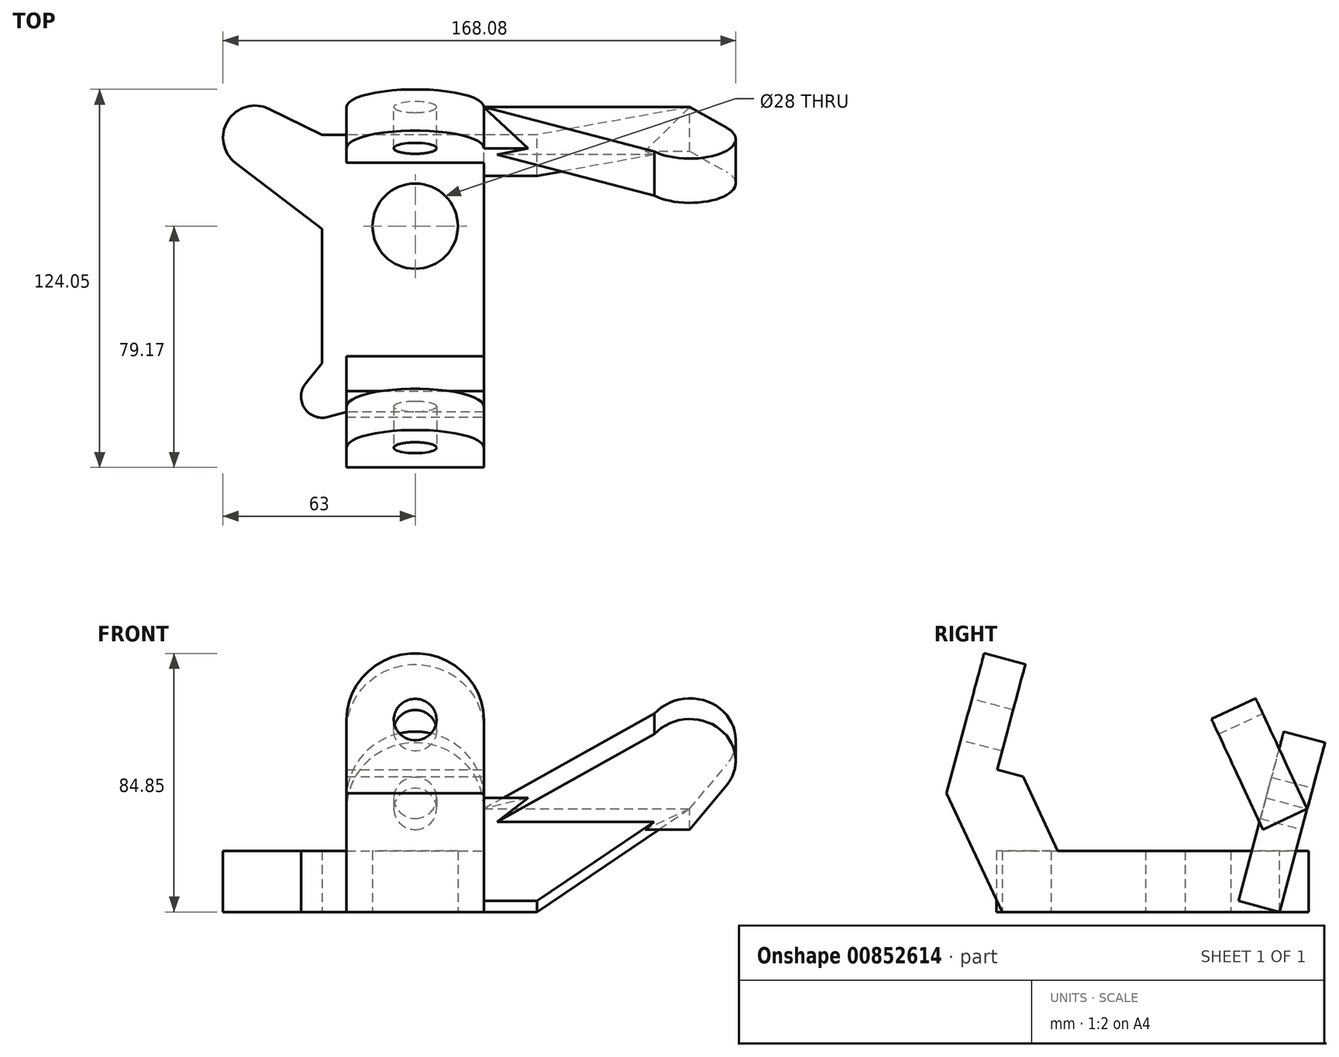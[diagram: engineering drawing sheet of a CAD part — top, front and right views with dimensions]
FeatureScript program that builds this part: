
annotation { "Feature Type Name" : "Feature", "Feature Type Description" : "" }
export const myFeature = defineFeature(function(context is Context, id is Id, definition is map)
    precondition{}
    {
        {
            var Q0;
            Q0=qCreatedBy(makeId("Top.planeOp"),FACE);
            var sketch = newSketch(context, id + "F0", { "sketchPlane" : qUnion([Q0])});
            skCircle(sketch, "E0", {"center": v(0, 15.5) * mm, "radius": 14 * mm});
            skLineSegment(sketch, "E1.bottom", {"start": v(22.5, 45.5) * mm, "end": v(-22.5, 45.5) * mm});
            skLineSegment(sketch, "E1.top", {"start": v(22.5, -45.5) * mm, "end": v(-22.5, -45.5) * mm});
            skLineSegment(sketch, "E1.left", {"start": v(22.5, 45.5) * mm, "end": v(22.5, -45.5) * mm});
            skLineSegment(sketch, "E1.right", {"start": v(-22.5, 45.5) * mm, "end": v(-22.5, -45.5) * mm});
            skPoint(sketch, "E1.middle", {"position": v(0, 0) * mm});
            skCircle(sketch, "E2", {"center": v(-52.5, 44.55) * mm, "radius": 10.5 * mm});
            skCircle(sketch, "E3", {"center": v(-30.5, -40.45) * mm, "radius": 6.91 * mm});
            skLineSegment(sketch, "E4", {"start": v(-30.5, -40.45) * mm, "end": v(-30.5, 14.55) * mm});
            skLineSegment(sketch, "E5", {"start": v(-30.5, 14.55) * mm, "end": v(-58.87, 36.2) * mm});
            skLineSegment(sketch, "E6", {"start": v(-30.5, 14.55) * mm, "end": v(-30.5, 45.5) * mm});
            skLineSegment(sketch, "E7", {"start": v(-30.5, 45.5) * mm, "end": v(-47.9, 53.98) * mm});
            skLineSegment(sketch, "E8", {"start": v(-30.5, 45.5) * mm, "end": v(-22.5, 45.5) * mm});
            skLineSegment(sketch, "E9", {"start": v(-30.5, -29.5) * mm, "end": v(-35.86, -36.1) * mm});
            skLineSegment(sketch, "E10", {"start": v(-22.5, -45.5) * mm, "end": v(-28.74, -47.14) * mm});
            skSolve(sketch);
        }
        {
            var Q0;
            {var subQ0=sQuery(id+"F0.wireOp",EDGE,"E5");Q0=makeQuery(id+"F0.imprint","IMPRINT",FACE,{"disambiguationData":[TD([[makeQuery(id+"F0.imprint","IMPRINT",EDGE,{"derivedFrom":subQ0}),-1.0]])]});}
            var Q1;
            {var subQ0=sQuery(id+"F0.wireOp",EDGE,"E2");var subQ1=makeQuery(id+"F0.imprint","INTERSECT",VERTEX,{"derivedFrom":[subQ0,sQuery(id+"F0.wireOp",EDGE,"E5")]});Q1=makeQuery(id+"F0.imprint","IMPRINT",FACE,{"disambiguationData":[TD([[makeQuery(id+"F0.imprint","IMPRINT",EDGE,{"disambiguationData":[TD([[subQ1,1.0]])],"derivedFrom":subQ0}),1.0]])]});}
            var Q2;
            Q2=makeQuery(id+"F0.imprint","IMPRINT",FACE,{"disambiguationData":[TD([[makeQuery(id+"F0.imprint","IMPRINT",EDGE,{"derivedFrom":sQuery(id+"F0.wireOp",EDGE,"E0")}),-1.0]])]});
            var Q3;
            Q3=makeQuery(id+"F0.imprint","IMPRINT",FACE,{"disambiguationData":[TD([[makeQuery(id+"F0.imprint","IMPRINT",EDGE,{"derivedFrom":sQuery(id+"F0.wireOp",EDGE,"E1.right")}),-1.0]])]});
            var Q4;
            {var subQ0=sQuery(id+"F0.wireOp",EDGE,"E3");var subQ1=makeQuery(id+"F0.imprint","INTERSECT",VERTEX,{"derivedFrom":[subQ0,sQuery(id+"F0.wireOp",EDGE,"E9")]});Q4=makeQuery(id+"F0.imprint","IMPRINT",FACE,{"disambiguationData":[TD([[makeQuery(id+"F0.imprint","IMPRINT",EDGE,{"disambiguationData":[TD([[subQ1,1.0]])],"derivedFrom":subQ0}),1.0]])]});}
            var Q5;
            {var subQ0=sQuery(id+"F0.wireOp",EDGE,"E9");Q5=makeQuery(id+"F0.imprint","IMPRINT",FACE,{"disambiguationData":[TD([[makeQuery(id+"F0.imprint","IMPRINT",EDGE,{"derivedFrom":subQ0}),1.0]])]});}
            extrude(context, id + "F1", {"entities" : qUnion([Q0, Q1, Q2, Q3, Q4, Q5]), "depth" : 20 * mm, "offsetDistance" : 25 * mm});
        }
        {
            var Q0;
            Q0=makeQuery(id+"F1.opExtrude","CAP_EDGE",EDGE,{"disambiguationData":[OSD([sQuery(id+"F0.wireOp",EDGE,"E1.bottom"),sQuery(id+"F0.wireOp",EDGE,"E8")])],"isStart":true});
            cPlane(context, id + "F2", {"entities" : qUnion([Q0]), "cplaneType" : CPlaneType.LINE_ANGLE, "offset" : 25 * mm, "angle" : 15 * degree, "width" : 150 * mm, "height" : 150 * mm});
        }
        {
            var Q0;
            Q0=qCreatedBy(id+"F2.planeOp",FACE);
            var sketch = newSketch(context, id + "F3", { "sketchPlane" : qUnion([Q0])});
            skCircle(sketch, "E11", {"center": v(0, 46.78) * mm, "radius": 22.5 * mm});
            skLineSegment(sketch, "E12", {"start": v(-22.5, 46.78) * mm, "end": v(-22.5, 11.78) * mm});
            skLineSegment(sketch, "E13", {"start": v(22.5, 46.78) * mm, "end": v(22.5, 11.78) * mm});
            skLineSegment(sketch, "E14", {"start": v(22.5, 11.78) * mm, "end": v(-22.5, 11.78) * mm});
            skCircle(sketch, "E15", {"center": v(0, 46.78) * mm, "radius": 7 * mm});
            skLineSegment(sketch, "E16", {"start": v(22.5, 46.78) * mm, "end": v(90, 46.78) * mm});
            skLineSegment(sketch, "E17", {"start": v(22.5, 11.78) * mm, "end": v(40, 11.78) * mm});
            skLineSegment(sketch, "E18", {"start": v(90, 46.78) * mm, "end": v(40, 11.78) * mm});
            skSolve(sketch);
        }
        {
            var Q0;
            Q0=makeQuery(id+"F3.imprint","IMPRINT",FACE,{"disambiguationData":[TD([[makeQuery(id+"F3.imprint","IMPRINT",EDGE,{"derivedFrom":sQuery(id+"F3.wireOp",EDGE,"E15")}),-1.0]])]});
            var Q1;
            {var subQ0=sQuery(id+"F3.wireOp",EDGE,"E12");Q1=makeQuery(id+"F3.imprint","IMPRINT",FACE,{"disambiguationData":[TD([[makeQuery(id+"F3.imprint","IMPRINT",EDGE,{"derivedFrom":subQ0}),1.0]])]});}
            var Q2;
            Q2=makeQuery(id+"F3.imprint","IMPRINT",FACE,{"disambiguationData":[TD([[makeQuery(id+"F3.imprint","IMPRINT",EDGE,{"derivedFrom":sQuery(id+"F3.wireOp",EDGE,"E13")}),1.0]])]});
            extrude(context, id + "F4", {"entities" : qUnion([Q0, Q1, Q2]), "operationType" : NewBodyOperationType.ADD, "depth" : 14 * mm, "offsetDistance" : 25 * mm});
        }
        {
            var Q0;
            Q0=makeQuery(id+"F4.opExtrude","CAP_EDGE",EDGE,{"disambiguationData":[OSD([sQuery(id+"F3.wireOp",EDGE,"E16")])],"isStart":true});
            cPlane(context, id + "F5", {"entities" : qUnion([Q0]), "cplaneType" : CPlaneType.LINE_ANGLE, "offset" : 25 * mm, "angle" : 25 * degree, "width" : 150 * mm, "height" : 150 * mm});
        }
        {
            var Q0;
            Q0=qCreatedBy(id+"F5.planeOp",FACE);
            var sketch = newSketch(context, id + "F6", { "sketchPlane" : qUnion([Q0])});
            skCircle(sketch, "E19", {"center": v(-90.08, 32.58) * mm, "radius": 15 * mm});
            skLineSegment(sketch, "E20", {"start": v(-90, 7.58) * mm, "end": v(-102.05, 23.54) * mm});
            skLineSegment(sketch, "E21", {"start": v(-78.48, 42.1) * mm, "end": v(-22.44, 7.58) * mm});
            skLineSegment(sketch, "E22", {"start": v(-22.44, 7.58) * mm, "end": v(-90, 7.58) * mm});
            skSolve(sketch);
        }
        {
            var Q0;
            {var subQ0=sQuery(id+"F6.wireOp",EDGE,"E20");Q0=makeQuery(id+"F6.imprint","IMPRINT",FACE,{"disambiguationData":[TD([[makeQuery(id+"F6.imprint","IMPRINT",EDGE,{"derivedFrom":subQ0}),-1.0]])]});}
            var Q1;
            {var subQ0=sQuery(id+"F6.wireOp",EDGE,"E19");var subQ1=makeQuery(id+"F6.imprint","INTERSECT",VERTEX,{"derivedFrom":[subQ0,sQuery(id+"F6.wireOp",EDGE,"E20")]});Q1=makeQuery(id+"F6.imprint","IMPRINT",FACE,{"disambiguationData":[TD([[makeQuery(id+"F6.imprint","IMPRINT",EDGE,{"disambiguationData":[TD([[subQ1,1.0]])],"derivedFrom":subQ0}),1.0]])]});}
            extrude(context, id + "F7", {"entities" : qUnion([Q0, Q1]), "operationType" : NewBodyOperationType.ADD, "oppositeDirection" : true, "depth" : 16 * mm, "offsetDistance" : 25 * mm});
        }
        {
            var Q0;
            Q0=makeQuery(id+"F1.opExtrude","CAP_EDGE",EDGE,{"disambiguationData":[OSD([sQuery(id+"F0.wireOp",EDGE,"E1.top")])],"isStart":true});
            cPlane(context, id + "F8", {"entities" : qUnion([Q0]), "cplaneType" : CPlaneType.LINE_ANGLE, "offset" : 25 * mm, "angle" : 25 * degree, "oppositeDirection" : true, "width" : 150 * mm, "height" : 150 * mm});
        }
        {
            var Q0;
            Q0=qCreatedBy(id+"F8.planeOp",FACE);
            var sketch = newSketch(context, id + "F9", { "sketchPlane" : qUnion([Q0])});
            skLineSegment(sketch, "E23", {"start": v(22.5, 19.23) * mm, "end": v(22.5, 62.23) * mm});
            skLineSegment(sketch, "E24", {"start": v(22.5, 19.23) * mm, "end": v(-22.5, 19.23) * mm});
            skLineSegment(sketch, "E25", {"start": v(-22.5, 19.23) * mm, "end": v(-22.5, 62.23) * mm});
            skLineSegment(sketch, "E26", {"start": v(-22.5, 62.23) * mm, "end": v(22.5, 62.23) * mm});
            skSolve(sketch);
        }
        {
            var Q0;
            Q0=makeQuery(id+"F9.imprint","IMPRINT",FACE,{"disambiguationData":[TD([[makeQuery(id+"F9.imprint","IMPRINT",EDGE,{"derivedFrom":sQuery(id+"F9.wireOp",EDGE,"E23")}),1.0]])]});
            extrude(context, id + "F10", {"entities" : qUnion([Q0]), "operationType" : NewBodyOperationType.ADD, "oppositeDirection" : true, "depth" : 25 * mm, "offsetDistance" : 25 * mm});
        }
        {
            var Q0;
            Q0=makeQuery(id+"F10.opExtrude","CAP_EDGE",EDGE,{"disambiguationData":[OSD([sQuery(id+"F9.wireOp",EDGE,"E26")])],"isStart":true});
            cPlane(context, id + "F11", {"entities" : qUnion([Q0]), "cplaneType" : CPlaneType.LINE_ANGLE, "offset" : 25 * mm, "angle" : 15 * degree, "oppositeDirection" : true, "width" : 150 * mm, "height" : 150 * mm});
        }
        {
            var Q0;
            Q0=qCreatedBy(id+"F11.planeOp",FACE);
            var sketch = newSketch(context, id + "F12", { "sketchPlane" : qUnion([Q0])});
            skCircle(sketch, "E27", {"center": v(0, 46.16) * mm, "radius": 22.5 * mm});
            skLineSegment(sketch, "E28", {"start": v(22.5, 46.16) * mm, "end": v(22.5, 21.16) * mm});
            skLineSegment(sketch, "E29", {"start": v(22.5, 21.16) * mm, "end": v(-22.5, 21.16) * mm});
            skLineSegment(sketch, "E30", {"start": v(-22.5, 46.16) * mm, "end": v(-22.5, 21.16) * mm});
            skCircle(sketch, "E31", {"center": v(0, 46.16) * mm, "radius": 7 * mm});
            skSolve(sketch);
        }
        {
            var Q0;
            {var subQ0=sQuery(id+"F12.wireOp",EDGE,"E27");var subQ1=makeQuery(id+"F12.imprint","INTERSECT",VERTEX,{"derivedFrom":[subQ0,sQuery(id+"F12.wireOp",EDGE,"E28")]});Q0=makeQuery(id+"F12.imprint","IMPRINT",FACE,{"disambiguationData":[TD([[makeQuery(id+"F12.imprint","IMPRINT",EDGE,{"disambiguationData":[TD([[subQ1,-1.0]])],"derivedFrom":subQ0}),1.0]])]});}
            var Q1;
            {var subQ0=sQuery(id+"F12.wireOp",EDGE,"E28");Q1=makeQuery(id+"F12.imprint","IMPRINT",FACE,{"disambiguationData":[TD([[makeQuery(id+"F12.imprint","IMPRINT",EDGE,{"derivedFrom":subQ0}),-1.0]])]});}
            extrude(context, id + "F13", {"entities" : qUnion([Q0, Q1]), "operationType" : NewBodyOperationType.ADD, "depth" : 14 * mm, "offsetDistance" : 25 * mm});
        }
        {
            var Q0;
            Q0=makeQuery(id+"F13.opExtrude","CAP_FACE",FACE,{"disambiguationData":[OSD([sQuery(id+"F12.wireOp",EDGE,"E27"),sQuery(id+"F12.wireOp",EDGE,"E28"),sQuery(id+"F12.wireOp",EDGE,"E29"),sQuery(id+"F12.wireOp",EDGE,"E30")])],"isStart":false});
            extrude(context, id + "F14", {"entities" : qUnion([Q0]), "operationType" : NewBodyOperationType.REMOVE, "depth" : 15.25 * mm, "offsetDistance" : 25 * mm});
        }
    });
